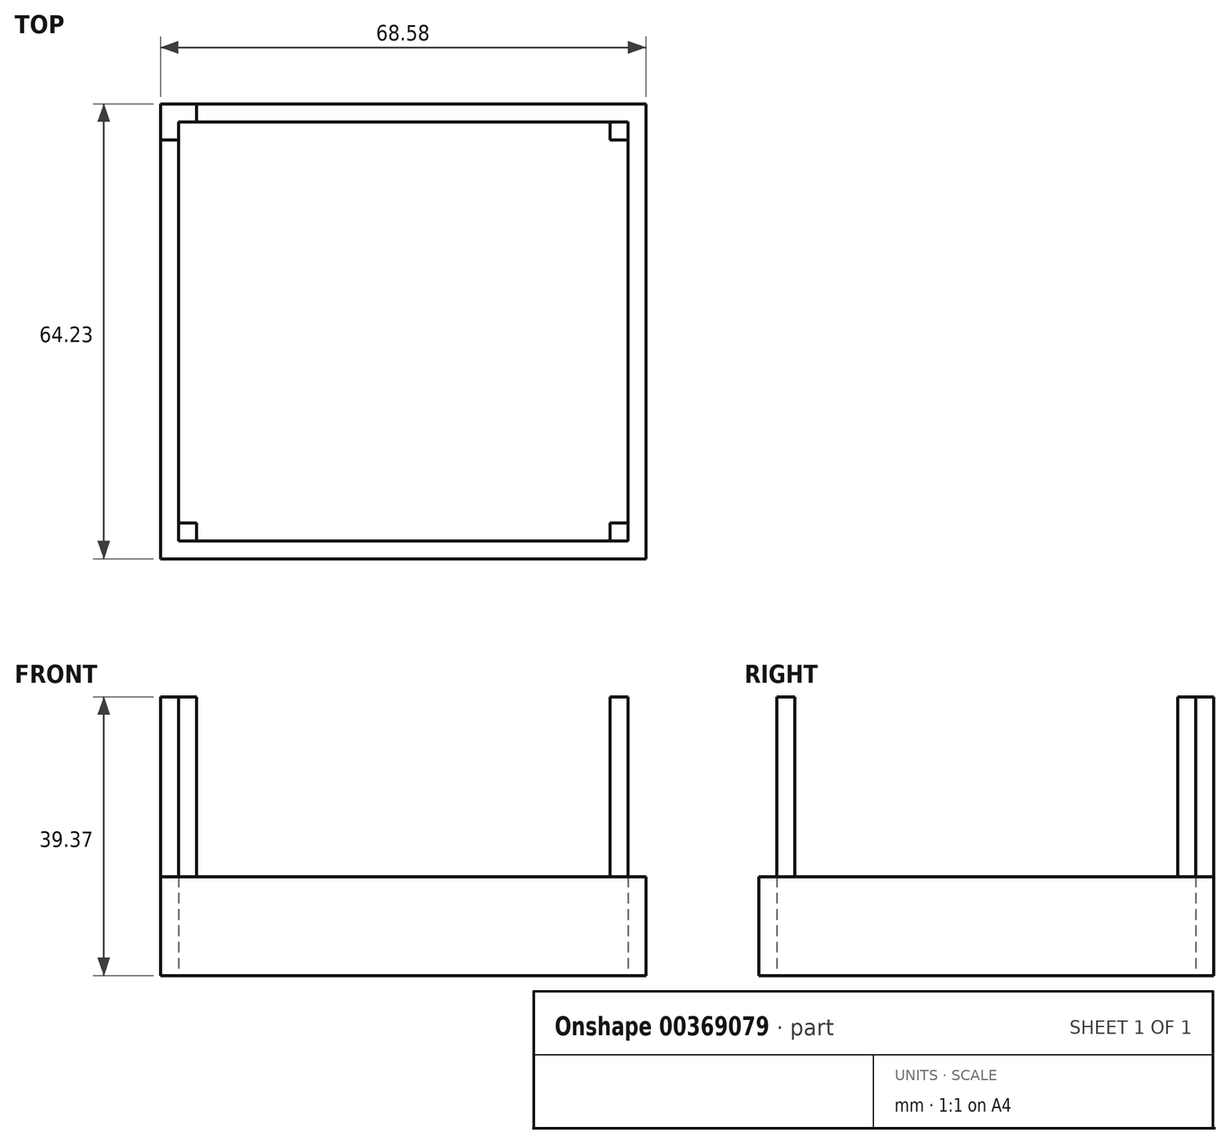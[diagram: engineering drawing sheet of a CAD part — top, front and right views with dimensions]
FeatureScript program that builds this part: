
annotation { "Feature Type Name" : "Feature", "Feature Type Description" : "" }
export const myFeature = defineFeature(function(context is Context, id is Id, definition is map)
    precondition{}
    {
        {
            var Q0;
            Q0=qCreatedBy(makeId("Top.planeOp"),FACE);
            var sketch = newSketch(context, id + "F0", { "sketchPlane" : qUnion([Q0])});
            skLineSegment(sketch, "E0.bottom", {"start": v(0, 0) * mm, "end": v(63.5, 0) * mm});
            skLineSegment(sketch, "E0.top", {"start": v(0, 59.15) * mm, "end": v(63.5, 59.15) * mm});
            skLineSegment(sketch, "E0.left", {"start": v(0, 0) * mm, "end": v(0, 59.15) * mm});
            skLineSegment(sketch, "E0.right", {"start": v(63.5, 0) * mm, "end": v(63.5, 59.15) * mm});
            skLineSegment(sketch, "E1", {"start": v(0, 0) * mm, "end": v(0, -2.54) * mm});
            skLineSegment(sketch, "E2", {"start": v(-2.54, 0) * mm, "end": v(-2.54, 61.69) * mm});
            skLineSegment(sketch, "E3", {"start": v(-2.54, 0) * mm, "end": v(-2.54, -2.54) * mm});
            skLineSegment(sketch, "E4", {"start": v(0, -2.54) * mm, "end": v(-2.54, -2.54) * mm});
            skLineSegment(sketch, "E5", {"start": v(0, -2.54) * mm, "end": v(66.04, -2.54) * mm});
            skLineSegment(sketch, "E6", {"start": v(63.5, 59.15) * mm, "end": v(63.5, 61.69) * mm});
            skLineSegment(sketch, "E7", {"start": v(-2.54, 61.69) * mm, "end": v(66.04, 61.69) * mm});
            skLineSegment(sketch, "E8", {"start": v(66.04, 59.15) * mm, "end": v(66.04, 61.69) * mm});
            skLineSegment(sketch, "E9", {"start": v(66.04, 61.69) * mm, "end": v(66.04, 59.15) * mm});
            skLineSegment(sketch, "E10", {"start": v(66.04, 59.15) * mm, "end": v(66.04, -2.54) * mm});
            skSolve(sketch);
        }
        {
            var Q0;
            Q0=makeQuery(id+"F0.imprint","IMPRINT",FACE,{"disambiguationData":[TD([[makeQuery(id+"F0.imprint","IMPRINT",EDGE,{"derivedFrom":sQuery(id+"F0.wireOp",EDGE,"E0.top")}),1.0]])]});
            var Q1;
            Q1=makeQuery(id+"F0.imprint","IMPRINT",FACE,{"disambiguationData":[TD([[makeQuery(id+"F0.imprint","IMPRINT",EDGE,{"derivedFrom":sQuery(id+"F0.wireOp",EDGE,"E0.bottom")}),-1.0]])]});
            extrude(context, id + "F1", {"entities" : qUnion([Q0, Q1]), "depth" : 1.27 * mm});
        }
        {
            var Q0;
            Q0=makeQuery(id+"F1.opExtrude","CAP_FACE",FACE,{"disambiguationData":[OSD([sQuery(id+"F0.wireOp",EDGE,"E0.bottom"),sQuery(id+"F0.wireOp",EDGE,"E0.top"),sQuery(id+"F0.wireOp",EDGE,"E0.left"),sQuery(id+"F0.wireOp",EDGE,"E0.right"),sQuery(id+"F0.wireOp",EDGE,"E2"),sQuery(id+"F0.wireOp",EDGE,"E3"),sQuery(id+"F0.wireOp",EDGE,"E4"),sQuery(id+"F0.wireOp",EDGE,"E5"),sQuery(id+"F0.wireOp",EDGE,"E7"),sQuery(id+"F0.wireOp",EDGE,"E9"),sQuery(id+"F0.wireOp",EDGE,"E10")])],"isStart":false});
            var sketch = newSketch(context, id + "F2", { "sketchPlane" : qUnion([Q0])});
            skLineSegment(sketch, "E11.bottom", {"start": v(-2.54, -2.54) * mm, "end": v(66.04, -2.54) * mm});
            skLineSegment(sketch, "E11.top", {"start": v(-2.54, 61.69) * mm, "end": v(66.04, 61.69) * mm});
            skLineSegment(sketch, "E11.left", {"start": v(-2.54, -2.54) * mm, "end": v(-2.54, 61.69) * mm});
            skLineSegment(sketch, "E11.right", {"start": v(66.04, -2.54) * mm, "end": v(66.04, 61.69) * mm});
            skLineSegment(sketch, "E12", {"start": v(2.54, 2.54) * mm, "end": v(2.54, 56.6) * mm});
            skLineSegment(sketch, "E13", {"start": v(2.54, 2.54) * mm, "end": v(60.96, 2.54) * mm});
            skLineSegment(sketch, "E14", {"start": v(60.96, 56.6) * mm, "end": v(60.96, 2.54) * mm});
            skLineSegment(sketch, "E15", {"start": v(60.96, 2.54) * mm, "end": v(60.96, 56.6) * mm});
            skLineSegment(sketch, "E16", {"start": v(60.96, 56.6) * mm, "end": v(2.54, 56.6) * mm});
            skLineSegment(sketch, "E17.trimOffspring", {"start": v(2.54, 56.6) * mm, "end": v(2.54, 2.54) * mm});
            skLineSegment(sketch, "E18.trimOffspring", {"start": v(60.96, 2.54) * mm, "end": v(2.54, 2.54) * mm});
            skSolve(sketch);
        }
        {
            var Q0;
            Q0=makeQuery(id+"F2.imprint","IMPRINT",FACE,{"disambiguationData":[TD([[makeQuery(id+"F2.imprint","IMPRINT",EDGE,{"derivedFrom":sQuery(id+"F2.wireOp",EDGE,"E15")}),-1.0]])]});
            var Q1;
            Q1=makeQuery(id+"F2.imprint","IMPRINT",FACE,{"disambiguationData":[TD([[makeQuery(id+"F2.imprint","IMPRINT",EDGE,{"derivedFrom":sQuery(id+"F2.wireOp",EDGE,"E11.bottom")}),-1.0]])]});
            extrude(context, id + "F3", {"entities" : qUnion([Q0, Q1]), "operationType" : NewBodyOperationType.ADD, "depth" : 12.7 * mm});
        }
        {
            var Q0;
            Q0=makeQuery(id+"F3.opExtrude","CAP_FACE",FACE,{"disambiguationData":[OSD([sQuery(id+"F2.wireOp",EDGE,"E11.bottom"),sQuery(id+"F2.wireOp",EDGE,"E11.top"),sQuery(id+"F2.wireOp",EDGE,"E11.left"),sQuery(id+"F2.wireOp",EDGE,"E11.right"),sQuery(id+"F2.wireOp",EDGE,"E15"),sQuery(id+"F2.wireOp",EDGE,"E16"),sQuery(id+"F2.wireOp",EDGE,"E17.trimOffspring"),sQuery(id+"F2.wireOp",EDGE,"E18.trimOffspring")])],"isStart":false});
            var sketch = newSketch(context, id + "F4", { "sketchPlane" : qUnion([Q0])});
            skLineSegment(sketch, "E19.bottom", {"start": v(-2.54, 61.69) * mm, "end": v(2.54, 61.69) * mm});
            skLineSegment(sketch, "E19.top", {"start": v(-2.54, 56.6) * mm, "end": v(2.54, 56.6) * mm});
            skLineSegment(sketch, "E19.left", {"start": v(-2.54, 61.69) * mm, "end": v(-2.54, 56.6) * mm});
            skLineSegment(sketch, "E19.right", {"start": v(2.54, 61.69) * mm, "end": v(2.54, 56.6) * mm});
            skLineSegment(sketch, "E20.bottom", {"start": v(60.96, 56.6) * mm, "end": v(66.04, 56.6) * mm});
            skLineSegment(sketch, "E20.top", {"start": v(60.96, 61.69) * mm, "end": v(66.04, 61.69) * mm});
            skLineSegment(sketch, "E20.left", {"start": v(60.96, 56.6) * mm, "end": v(60.96, 61.69) * mm});
            skLineSegment(sketch, "E20.right", {"start": v(66.04, 56.6) * mm, "end": v(66.04, 61.69) * mm});
            skLineSegment(sketch, "E21.bottom", {"start": v(60.96, 2.54) * mm, "end": v(66.04, 2.54) * mm});
            skLineSegment(sketch, "E21.top", {"start": v(60.96, -2.54) * mm, "end": v(66.04, -2.54) * mm});
            skLineSegment(sketch, "E21.left", {"start": v(60.96, 2.54) * mm, "end": v(60.96, -2.54) * mm});
            skLineSegment(sketch, "E21.right", {"start": v(66.04, 2.54) * mm, "end": v(66.04, -2.54) * mm});
            skLineSegment(sketch, "E22.bottom", {"start": v(2.54, 2.54) * mm, "end": v(-2.54, 2.54) * mm});
            skLineSegment(sketch, "E22.top", {"start": v(2.54, -2.54) * mm, "end": v(-2.54, -2.54) * mm});
            skLineSegment(sketch, "E22.left", {"start": v(2.54, 2.54) * mm, "end": v(2.54, -2.54) * mm});
            skLineSegment(sketch, "E22.right", {"start": v(-2.54, 2.54) * mm, "end": v(-2.54, -2.54) * mm});
            skSolve(sketch);
        }
        {
            var Q0;
            Q0=makeQuery(id+"F4.imprint","IMPRINT",FACE,{"disambiguationData":[TD([[makeQuery(id+"F4.imprint","IMPRINT",EDGE,{"derivedFrom":sQuery(id+"F4.wireOp",EDGE,"E19.bottom")}),-1.0]])]});
            var Q1;
            Q1=makeQuery(id+"F4.imprint","IMPRINT",FACE,{"disambiguationData":[TD([[makeQuery(id+"F4.imprint","IMPRINT",EDGE,{"derivedFrom":sQuery(id+"F4.wireOp",EDGE,"E22.bottom")}),1.0]])]});
            var Q2;
            Q2=makeQuery(id+"F4.imprint","IMPRINT",FACE,{"disambiguationData":[TD([[makeQuery(id+"F4.imprint","IMPRINT",EDGE,{"derivedFrom":sQuery(id+"F4.wireOp",EDGE,"E21.bottom")}),-1.0]])]});
            var Q3;
            Q3=makeQuery(id+"F4.imprint","IMPRINT",FACE,{"disambiguationData":[TD([[makeQuery(id+"F4.imprint","IMPRINT",EDGE,{"derivedFrom":sQuery(id+"F4.wireOp",EDGE,"E20.bottom")}),1.0]])]});
            extrude(context, id + "F5", {"entities" : qUnion([Q0, Q1, Q2, Q3]), "operationType" : NewBodyOperationType.ADD, "depth" : 25.4 * mm});
        }
    });
